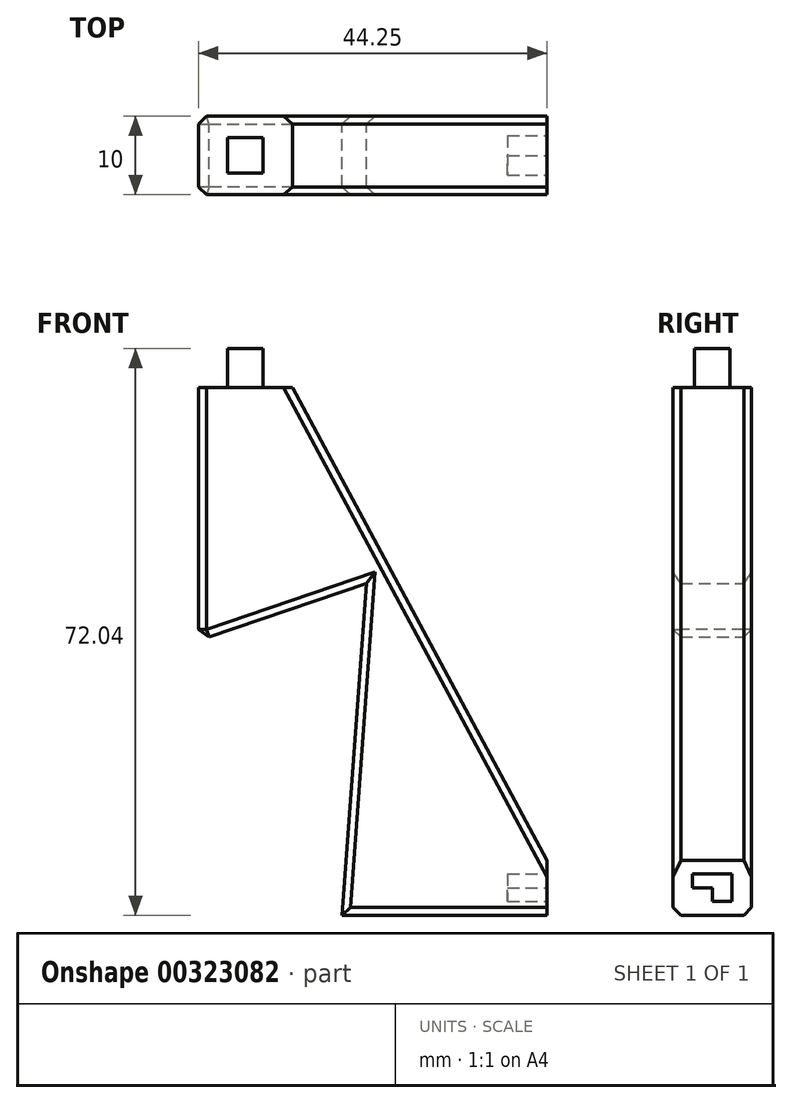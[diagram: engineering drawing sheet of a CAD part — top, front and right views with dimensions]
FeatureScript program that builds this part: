
annotation { "Feature Type Name" : "Feature", "Feature Type Description" : "" }
export const myFeature = defineFeature(function(context is Context, id is Id, definition is map)
    precondition{}
    {
        {
            var Q0;
            Q0=qCreatedBy(makeId("Front.planeOp"),FACE);
            var sketch = newSketch(context, id + "F0", { "sketchPlane" : qUnion([Q0])});
            skLineSegment(sketch, "E0", {"start": v(-55.59, 49.1) * mm, "end": v(-55.59, 17) * mm});
            skLineSegment(sketch, "E1", {"start": v(-55.59, 17) * mm, "end": v(-34.3, 24.26) * mm});
            skLineSegment(sketch, "E2", {"start": v(-34.3, 24.26) * mm, "end": v(-37.39, -17.93) * mm});
            skLineSegment(sketch, "E3", {"start": v(-11.34, -17.93) * mm, "end": v(-37.39, -17.93) * mm});
            skLineSegment(sketch, "E4", {"start": v(-11.34, -17.93) * mm, "end": v(-11.34, -10.93) * mm});
            skLineSegment(sketch, "E5", {"start": v(-55.59, 49.1) * mm, "end": v(-43.69, 49.1) * mm});
            skLineSegment(sketch, "E6", {"start": v(-11.34, -10.93) * mm, "end": v(-43.69, 49.1) * mm});
            skSolve(sketch);
        }
        {
            var Q0;
            Q0=makeQuery(id+"F0.imprint","IMPRINT",FACE,{"disambiguationData":[TD([[makeQuery(id+"F0.imprint","IMPRINT",EDGE,{"derivedFrom":sQuery(id+"F0.wireOp",EDGE,"E0")}),1.0]])]});
            extrude(context, id + "F1", {"entities" : qUnion([Q0]), "depth" : 10 * mm});
        }
        {
            var Q0;
            Q0=makeQuery(id+"F1.opExtrude","SWEPT_FACE",FACE,{"disambiguationData":[OSD([sQuery(id+"F0.wireOp",EDGE,"E4")])]});
            var sketch = newSketch(context, id + "F2", { "sketchPlane" : qUnion([Q0])});
            skLineSegment(sketch, "E7", {"start": v(-5, -17.93) * mm, "end": v(-5, -10.93) * mm});
            skLineSegment(sketch, "E8", {"start": v(-10, -14.43) * mm, "end": v(0, -14.43) * mm});
            skLineSegment(sketch, "E9.bottom", {"start": v(-2.5, -12.68) * mm, "end": v(-7.5, -12.68) * mm});
            skLineSegment(sketch, "E9.top", {"start": v(-2.5, -16.18) * mm, "end": v(-7.5, -16.18) * mm});
            skLineSegment(sketch, "E9.left", {"start": v(-2.5, -12.68) * mm, "end": v(-2.5, -16.18) * mm});
            skLineSegment(sketch, "E9.right", {"start": v(-7.5, -12.68) * mm, "end": v(-7.5, -16.18) * mm});
            skPoint(sketch, "E9.middle", {"position": v(-5, -14.43) * mm});
            skSolve(sketch);
        }
        {
            var Q0;
            {var subQ0=sQuery(id+"F2.wireOp",EDGE,"E9.top");var subQ1=sQuery(id+"F2.wireOp",EDGE,"E7");var subQ2=makeQuery(id+"F2.imprint","INTERSECT",VERTEX,{"derivedFrom":[subQ1,subQ0]});Q0=makeQuery(id+"F2.imprint","IMPRINT",FACE,{"disambiguationData":[TD([[makeQuery(id+"F2.imprint","IMPRINT",EDGE,{"disambiguationData":[TD([[subQ2,-1.0]])],"derivedFrom":subQ1}),1.0]])]});}
            var sketch = newSketch(context, id + "F3", { "sketchPlane" : qUnion([Q0])});
            skSolve(sketch);
        }
        {
            var Q0;
            {var subQ0=sQuery(id+"F2.wireOp",EDGE,"E8");var subQ1=sQuery(id+"F2.wireOp",EDGE,"E7");var subQ2=makeQuery(id+"F2.imprint","INTERSECT",VERTEX,{"derivedFrom":[subQ1,subQ0]});Q0=makeQuery(id+"F2.imprint","IMPRINT",FACE,{"disambiguationData":[TD([[makeQuery(id+"F2.imprint","IMPRINT",EDGE,{"disambiguationData":[TD([[subQ2,-1.0]])],"derivedFrom":subQ1}),1.0]])]});}
            var Q1;
            {var subQ0=sQuery(id+"F2.wireOp",EDGE,"E8");var subQ1=sQuery(id+"F2.wireOp",EDGE,"E7");var subQ2=makeQuery(id+"F2.imprint","INTERSECT",VERTEX,{"derivedFrom":[subQ1,subQ0]});Q1=makeQuery(id+"F2.imprint","IMPRINT",FACE,{"disambiguationData":[TD([[makeQuery(id+"F2.imprint","IMPRINT",EDGE,{"disambiguationData":[TD([[subQ2,-1.0]])],"derivedFrom":subQ1}),-1.0]])]});}
            var Q2;
            {var subQ0=sQuery(id+"F2.wireOp",EDGE,"E9.top");var subQ1=sQuery(id+"F2.wireOp",EDGE,"E7");var subQ2=makeQuery(id+"F2.imprint","INTERSECT",VERTEX,{"derivedFrom":[subQ1,subQ0]});Q2=makeQuery(id+"F3.imprint","IMPRINT",FACE,{"disambiguationData":[TD([[makeQuery(id+"F3.imprint","IMPRINT",EDGE,{"derivedFrom":makeQuery(id+"F2.imprint","IMPRINT",EDGE,{"disambiguationData":[TD([[subQ2,-1.0]])],"derivedFrom":subQ1})}),1.0]])]});}
            var Q3;
            {var subQ0=sQuery(id+"F2.wireOp",EDGE,"E9.top");var subQ1=sQuery(id+"F2.wireOp",EDGE,"E7");var subQ2=makeQuery(id+"F2.imprint","INTERSECT",VERTEX,{"derivedFrom":[subQ1,subQ0]});Q3=makeQuery(id+"F2.imprint","IMPRINT",FACE,{"disambiguationData":[TD([[makeQuery(id+"F2.imprint","IMPRINT",EDGE,{"disambiguationData":[TD([[subQ2,-1.0]])],"derivedFrom":subQ1}),-1.0]])]});}
            extrude(context, id + "F4", {"entities" : qUnion([Q0, Q1, Q2, Q3]), "operationType" : NewBodyOperationType.REMOVE, "oppositeDirection" : true, "depth" : 5 * mm});
        }
        {
            var Q0;
            Q0=makeQuery(id+"F1.opExtrude","CAP_EDGE",EDGE,{"disambiguationData":[OSD([sQuery(id+"F0.wireOp",EDGE,"E0")])],"isStart":false});
            var Q1;
            Q1=makeQuery(id+"F1.opExtrude","SWEPT_EDGE",EDGE,{"disambiguationData":[OSD([sQuery(id+"F0.wireOp",EDGE,"E0"),sQuery(id+"F0.wireOp",EDGE,"E1")])]});
            var Q2;
            Q2=makeQuery(id+"F1.opExtrude","CAP_EDGE",EDGE,{"disambiguationData":[OSD([sQuery(id+"F0.wireOp",EDGE,"E0")])],"isStart":true});
            var Q3;
            Q3=makeQuery(id+"F1.opExtrude","CAP_EDGE",EDGE,{"disambiguationData":[OSD([sQuery(id+"F0.wireOp",EDGE,"E1")])],"isStart":false});
            var Q4;
            Q4=makeQuery(id+"F1.opExtrude","CAP_EDGE",EDGE,{"disambiguationData":[OSD([sQuery(id+"F0.wireOp",EDGE,"E1")])],"isStart":true});
            var Q5;
            Q5=makeQuery(id+"F1.opExtrude","CAP_EDGE",EDGE,{"disambiguationData":[OSD([sQuery(id+"F0.wireOp",EDGE,"E2")])],"isStart":false});
            var Q6;
            Q6=makeQuery(id+"F1.opExtrude","CAP_EDGE",EDGE,{"disambiguationData":[OSD([sQuery(id+"F0.wireOp",EDGE,"E2")])],"isStart":true});
            var Q7;
            Q7=makeQuery(id+"F1.opExtrude","CAP_EDGE",EDGE,{"disambiguationData":[OSD([sQuery(id+"F0.wireOp",EDGE,"E6")])],"isStart":false});
            var Q8;
            Q8=makeQuery(id+"F1.opExtrude","CAP_EDGE",EDGE,{"disambiguationData":[OSD([sQuery(id+"F0.wireOp",EDGE,"E6")])],"isStart":true});
            var Q9;
            Q9=makeQuery(id+"F1.opExtrude","CAP_EDGE",EDGE,{"disambiguationData":[OSD([sQuery(id+"F0.wireOp",EDGE,"E3")])],"isStart":false});
            var Q10;
            Q10=makeQuery(id+"F1.opExtrude","CAP_EDGE",EDGE,{"disambiguationData":[OSD([sQuery(id+"F0.wireOp",EDGE,"E3")])],"isStart":true});
            chamfer(context, id + "F5", {"entities" : qUnion([Q0, Q1, Q2, Q3, Q4, Q5, Q6, Q7, Q8, Q9, Q10]), "width" : 1 * mm, "tangentPropagation" : true});
        }
        {
            var Q0;
            Q0=makeQuery(id+"F1.opExtrude","SWEPT_FACE",FACE,{"disambiguationData":[OSD([sQuery(id+"F0.wireOp",EDGE,"E5")])]});
            var sketch = newSketch(context, id + "F6", { "sketchPlane" : qUnion([Q0])});
            skLineSegment(sketch, "E10", {"start": v(-49.7, -10) * mm, "end": v(-49.7, 0) * mm});
            skLineSegment(sketch, "E11", {"start": v(-55.59, -5) * mm, "end": v(-43.69, -5) * mm});
            skLineSegment(sketch, "E12.bottom", {"start": v(-47.39, -2.75) * mm, "end": v(-51.89, -2.75) * mm});
            skLineSegment(sketch, "E12.top", {"start": v(-47.39, -7.25) * mm, "end": v(-51.89, -7.25) * mm});
            skLineSegment(sketch, "E12.left", {"start": v(-47.39, -2.75) * mm, "end": v(-47.39, -7.25) * mm});
            skLineSegment(sketch, "E12.right", {"start": v(-51.89, -2.75) * mm, "end": v(-51.89, -7.25) * mm});
            skPoint(sketch, "E12.middle", {"position": v(-49.64, -5) * mm});
            skSolve(sketch);
        }
        {
            var Q0;
            {var subQ0=sQuery(id+"F6.wireOp",EDGE,"E12.top");var subQ1=sQuery(id+"F6.wireOp",EDGE,"E10");var subQ2=makeQuery(id+"F6.imprint","INTERSECT",VERTEX,{"derivedFrom":[subQ1,subQ0]});Q0=makeQuery(id+"F6.imprint","IMPRINT",FACE,{"disambiguationData":[TD([[makeQuery(id+"F6.imprint","IMPRINT",EDGE,{"disambiguationData":[TD([[subQ2,-1.0]])],"derivedFrom":subQ1}),-1.0]])]});}
            var Q1;
            {var subQ0=sQuery(id+"F6.wireOp",EDGE,"E12.top");var subQ1=sQuery(id+"F6.wireOp",EDGE,"E10");var subQ2=makeQuery(id+"F6.imprint","INTERSECT",VERTEX,{"derivedFrom":[subQ1,subQ0]});Q1=makeQuery(id+"F6.imprint","IMPRINT",FACE,{"disambiguationData":[TD([[makeQuery(id+"F6.imprint","IMPRINT",EDGE,{"disambiguationData":[TD([[subQ2,-1.0]])],"derivedFrom":subQ1}),1.0]])]});}
            var Q2;
            {var subQ0=sQuery(id+"F6.wireOp",EDGE,"E11");var subQ1=sQuery(id+"F6.wireOp",EDGE,"E10");var subQ2=makeQuery(id+"F6.imprint","INTERSECT",VERTEX,{"derivedFrom":[subQ1,subQ0]});Q2=makeQuery(id+"F6.imprint","IMPRINT",FACE,{"disambiguationData":[TD([[makeQuery(id+"F6.imprint","IMPRINT",EDGE,{"disambiguationData":[TD([[subQ2,-1.0]])],"derivedFrom":subQ1}),1.0]])]});}
            var Q3;
            {var subQ0=sQuery(id+"F6.wireOp",EDGE,"E11");var subQ1=sQuery(id+"F6.wireOp",EDGE,"E10");var subQ2=makeQuery(id+"F6.imprint","INTERSECT",VERTEX,{"derivedFrom":[subQ1,subQ0]});Q3=makeQuery(id+"F6.imprint","IMPRINT",FACE,{"disambiguationData":[TD([[makeQuery(id+"F6.imprint","IMPRINT",EDGE,{"disambiguationData":[TD([[subQ2,-1.0]])],"derivedFrom":subQ1}),-1.0]])]});}
            extrude(context, id + "F7", {"entities" : qUnion([Q0, Q1, Q2, Q3]), "operationType" : NewBodyOperationType.ADD, "depth" : 5 * mm});
        }
    });
